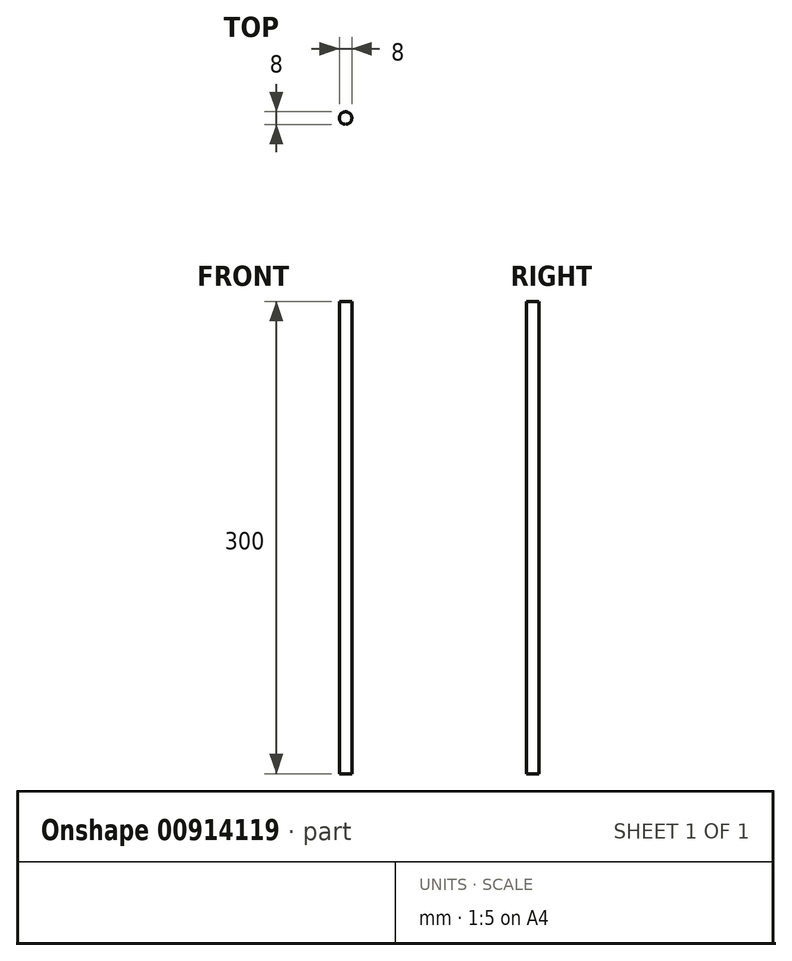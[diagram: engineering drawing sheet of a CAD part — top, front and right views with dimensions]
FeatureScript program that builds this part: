
annotation { "Feature Type Name" : "Feature", "Feature Type Description" : "" }
export const myFeature = defineFeature(function(context is Context, id is Id, definition is map)
    precondition{}
    {
        {
            var Q0;
            Q0=qCreatedBy(makeId("Top.planeOp"),FACE);
            var sketch = newSketch(context, id + "F0", { "sketchPlane" : qUnion([Q0])});
            skCircle(sketch, "E0", {"center": v(0, 0) * mm, "radius": 4 * mm});
            skSolve(sketch);
        }
        {
            var Q0;
            Q0 = qSketchRegion(id + "F0", true);
            extrude(context, id + "F1", {"entities" : qUnion([Q0]), "depth" : 300 * mm, "offsetDistance" : 25 * mm});
        }
    });
